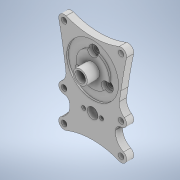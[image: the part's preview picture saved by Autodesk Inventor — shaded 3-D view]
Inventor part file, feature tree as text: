
AUTODESK INVENTOR PART (.ipt)
format: ipt  version: 2022 (Build 260153070, 153G)  size: 271,872 bytes
history: native  units: mm
features: reference x10, extrude x6, other x5, sketch x4
ambient origin geometry x8: Origin, YZ Plane, XZ Plane, XY Plane, X Axis, Y Axis, Z Axis, Center Point
bodies: Solid1 (feature_tree)
feature tree (25):
  extrude  "Extrusion1"  Depth=4.0mm
  sketch  "Sketch2"  dims[d2=4.0mm d3=3.1mm]
  extrude  "Extrusion2"  Depth=4.0mm
  extrude  "Extrusion3"  Depth=1.5mm
  extrude  "Extrusion4"  Depth=1.5mm
  extrude  "Extrusion5"  Depth=4.0mm
  extrude  "Extrusion6"  Depth=4.0mm
  sketch  "Sketch1"  dims[d0=12.3mm d1=4.0mm]
  reference  "Reference1"
  reference  "Reference2"
  reference  "Reference3"
  reference  "Reference5"
  reference  "Reference6"
  reference  "Reference7"
  reference  "Reference8"
  reference  "Reference9"
  reference  "Reference10"
  reference  "Reference11"
  sketch  "Sketch4"  dims[d4=1.5mm d5=3.1mm d6=1.5mm]
  sketch  "Sketch5"  dims[d7=3.1mm d8=1.5mm d9=3.1mm d10=1.5mm d11=32.0mm d12=50.0mm d14=50.0mm d17=4.0mm d18=0.0mm d19=16.0mm d20=37.0mm d21=1.0mm d22=2.0mm d23=0.0mm d24=7.0mm d25=0.0mm d26=1.75mm d27=3.5mm d28=1.0mm d29=0.0mm d30=30.0mm d32=360.0deg d34=2.5mm d35=0.0mm d38=17.25mm d40=1.5mm d42=4.0mm d43=0.0mm d45=25.307274mm]
  other  "<userpath> laptop\Desktop\SumoBot\sumobotLIDAR\sumobotLIDAR.iam"
  other  "sumobotLIDAR.iam"
  other  "SRM-12-06A:1"
  other  "MOTOR:1"
  other  "608ZZ bearing:1"
